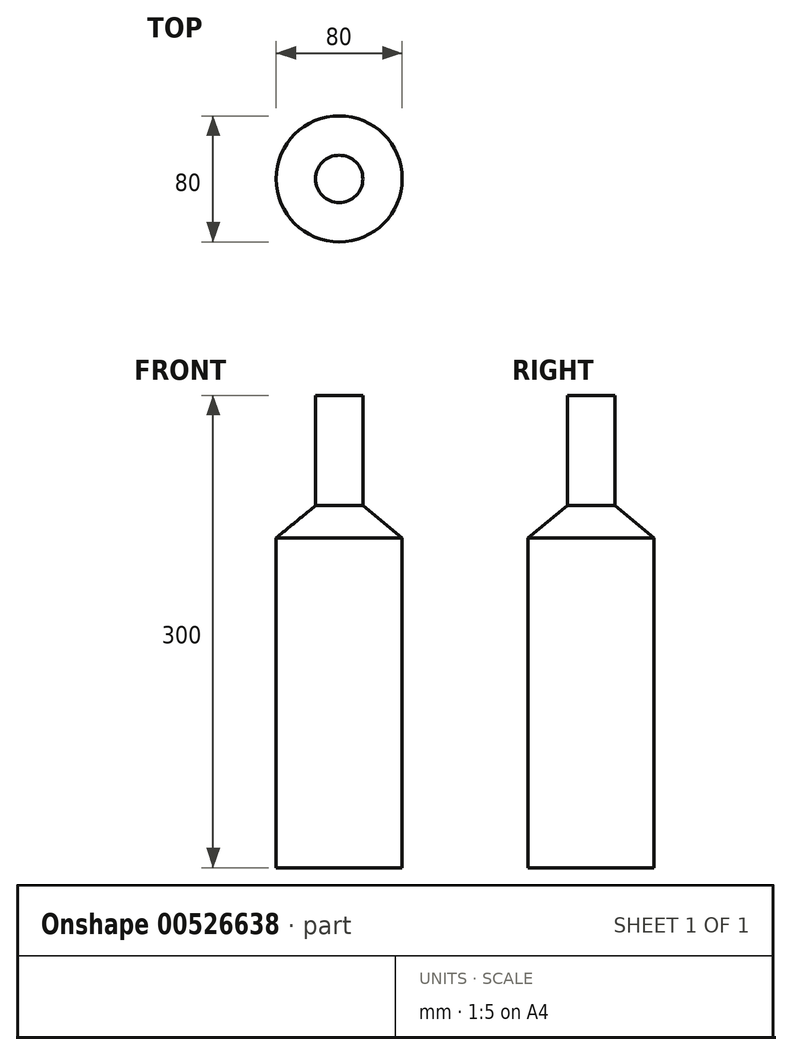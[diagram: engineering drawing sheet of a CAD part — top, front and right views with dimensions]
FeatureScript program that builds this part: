
annotation { "Feature Type Name" : "Feature", "Feature Type Description" : "" }
export const myFeature = defineFeature(function(context is Context, id is Id, definition is map)
    precondition{}
    {
        {
            var Q0;
            Q0=qCreatedBy(makeId("Front.planeOp"),FACE);
            var sketch = newSketch(context, id + "F0", { "sketchPlane" : qUnion([Q0])});
            skLineSegment(sketch, "E0", {"start": v(0, 114.93) * mm, "end": v(15, 114.93) * mm});
            skLineSegment(sketch, "E1", {"start": v(15, 114.93) * mm, "end": v(15, 44.93) * mm});
            skLineSegment(sketch, "E2", {"start": v(40, 24.4) * mm, "end": v(40, -185.07) * mm});
            skLineSegment(sketch, "E3", {"start": v(40, -185.07) * mm, "end": v(0, -185.07) * mm});
            skLineSegment(sketch, "E4", {"start": v(15, 44.93) * mm, "end": v(40, 24.4) * mm});
            skLineSegment(sketch, "E5", {"start": v(0, -185.07) * mm, "end": v(0, 114.93) * mm});
            skSolve(sketch);
        }
        {
            var Q0;
            Q0=makeQuery(id+"F0.imprint","IMPRINT",FACE,{"disambiguationData":[TD([[makeQuery(id+"F0.imprint","IMPRINT",EDGE,{"derivedFrom":sQuery(id+"F0.wireOp",EDGE,"E0")}),-1.0]])]});
            var Q1;
            Q1=sQuery(id+"F0.wireOp",EDGE,"E5");
            revolve(context, id + "F1", {"entities" : qUnion([Q0]), "axis" : qUnion([Q1]), "revolveType" : RevolveType.FULL});
        }
    });
